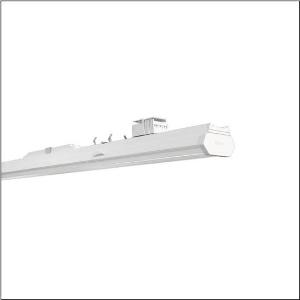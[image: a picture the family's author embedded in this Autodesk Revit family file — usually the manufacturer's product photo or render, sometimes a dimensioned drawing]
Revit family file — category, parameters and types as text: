
# Revit family: licross_11_protected_mo_51td1bdn59xg
name_source: partatom
category: Lighting Fixtures
units: mm (PartAtom-declared; Revit-internal decimal feet)

## family parameters
Cut with Voids When Loaded = No
Host = Face
Light Source = No
Part Type = Normal
Room Calculation Point = No
Round Connector Dimension = Use Diameter
Shared = No

## types (1)
- --- (1 x LED, 9230 lm, 57.1 W, 5000K)
    Apparent Load = 57 VA
    CIE Flux Codes = 54 82 95 97 100
    Color Rendering = 80
    Color Temperature = 5000K
    Default Elevation = 1800 mm
    Description = Licross 11 Protected MO, luminaire insert, of sheet steel, galvanised, coil coated, white, length: 1.500mm, width: 90mm, height: 101mm, LED rated luminous flux: 9.230lm, light colour: 850, SDCM (Standard Deviation of Colour Matching)MacAdam ≤ 2 SDCM (initial), control gear: DALI 2, with plug, 5-pole, with phase selection, mains connection: 220..240V, AC, 50/60Hz, rated input power: 57W, internal wiring halogen-free, primary optical cover: cover, of PMMA, light emission: direct distribution, primary light characteristic: symmetric, protection rating (complete): IP54, insulation class (complete): insulation class I (protective earthing), certification: CE, ENEC, VDE, UKCA, protection symbol: D if used in an environment with non-conductive dust loads with corresponding accessories, impact resistance: IK06, permissible ambient temperature for indoor applications: -25..+35°C, corresponds to IFS (International Featured Standards) requirements for safety and quality in the food industry, reducing of maximum allowable ambient temperature of 5°C with ceiling mounting, LABS conformity tested according to VDMA 24364:2018-05, The light source and the operating device comply with the requirements of the Ecodesign Regulation (EU) 2019/2020 and are replaceable in accordance with this regulation, packaging unit: 1 piece
    Height = 92 mm
    Lamp = 1 x LED
    Lamp Light Flux = 9230 lm
    Lamp Power = 57.1 W
    Lamp count = 1
    Length = 1500 mm
    Luminous efficacy = 162 lm/W
    Manufacturer = Siteco
    ModVariant = No
    Model = 51TD1BDN59XG
    Mounting Place = Ceiling
    Mounting Type = Pendant
    Number of Poles = 1
    OnlyDefault = Yes
    Power Factor = 1
    Product Name = Licross 11 Protected MO
    Product group = luminaire insert | ceiling pendant
    ProductGroupID = 901
    Protection Class = Protection class I
    Protection Degree = IP 54
    RLX_Detail_Level = 1
    RLX_Emergency_Light_Flux = 0 lm
    RLX_Emergency_Type = 0
    RLX_Emergency_Type_DB = No
    RlxData = <blob elided: 24601 chars, md5=b172b119>
    Socket = socket
    Standby Power = 0 W
    System Light Flux = 9230 lm
    System Power = 57 W
    Type Comments = factory setting: luminous flux: 100 % | dim-lin: 254 | 378 mA
    Type Image = l_1256145.jpg
    URL = http://relux.com
    VarID = @adj_021435
    Voltage = 0 V
    Weight = 0.00 kg
    Width = 88 mm

## geometry (parser evidence)
native form markers: Blend x4, Sweep x9
no freeform markers — native parametric forms only
